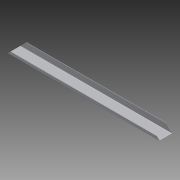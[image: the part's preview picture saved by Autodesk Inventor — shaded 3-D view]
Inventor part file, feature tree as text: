
AUTODESK INVENTOR PART (.ipt)
format: ipt  version: 2013 (Build 170138000, 138)  size: 192,000 bytes
history: native  units: in
note: dims shown in document units (in); Inventor stores cm internally (conversion verified against a paired STEP export)
features: sheet_metal_op x7, other x4, projected_geometry x3, sketch x2, extrude x1
ambient origin geometry x8: Origin, YZ Plane, XZ Plane, XY Plane, X Axis, Y Axis, Z Axis, Center Point
bodies: Solid1 (feature_tree)
feature tree (17):
  sheet_metal_op  "Face1"
  sheet_metal_op  "Flange1"
  sheet_metal_op  "Flange2"
  extrude  "Extrusion4"  Depth=4.0in
  sketch  "Sketch1"  dims[d0=48.0in d1=4.0in]
  other  "Plate1"
  other  "Plate2"
  sheet_metal_op  "Bend1"
  sheet_metal_op  "Corner1"
  other  "Plate3"
  sheet_metal_op  "Bend2"
  sheet_metal_op  "Corner2"
  sketch  "Sketch5"  dims[d2=0.0938in d3=0.0938in d4=0.0469in d5=0.1875in d6=0.0938in d7=2.0in d8=90.0deg d9=0.0938in d10=0.375in d11=0.0938in d12=0.0938in d13=0.0938in d14=0.0469in d15=0.1875in d16=0.0938in d17=1.0in d18=90.0deg d19=0.0938in d20=0.375in d21=0.0938in d22=0.0938in d39=45.0deg d40=45.0deg d41=1.0in d42=0.0in]
  projected_geometry  "Projected Loop1"
  projected_geometry  "Projected Loop2"
  projected_geometry  "Projected Loop3"
  other  "Definition1"
